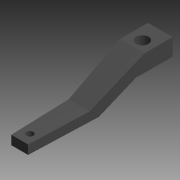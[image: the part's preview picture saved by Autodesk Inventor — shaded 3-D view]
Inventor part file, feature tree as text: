
AUTODESK INVENTOR PART (.ipt)
format: ipt  version: 2015 (Build 190159000, 159)  size: 88,576 bytes
history: native  units: mm (DEFAULTED — no unit token found)
features: chamfer x2, hole x2, extrude x1, sketch x1
ambient origin geometry x8: Origin, YZ Plane, XZ Plane, XY Plane, X Axis, Y Axis, Z Axis, Center Point
bodies: Solid1 (feature_tree)
feature tree (6):
  extrude  "Extrusion1"  Depth=125.0mm
  chamfer  "Chamfer1"  Distance=25.0mm
  chamfer  "Chamfer2"  Distance=30.0mm
  hole  "Hole1"  [1 undecoded]
  hole  "Hole2"  [1 undecoded]
  sketch  "Sketch1"  dims[d0=8.0mm d1=125.0mm d2=25.0mm d3=30.0mm d4=15.0mm d5=27.052603mm d6=22.0mm d7=0.0mm d8=100.0mm d9=3.5mm d10=45.0deg d11=100.0mm d12=3.5mm d13=45.0deg d14=9.0mm d15=11.0mm d16=6.0mm d17=6.0mm d18=4.0mm d19=2.0mm d20=90.0deg d21=8.0mm d22=20.594885mm d23=16.0mm d24=11.0mm d25=11.0mm d26=6.0mm d27=4.0mm d28=2.0mm d29=90.0deg d30=8.0mm d31=20.594885mm]
note: 2 required parameter values undecoded (feature->parameter linkage not recoverable at this tier; creation-order binding heuristic only, values carry confidence <= 0.55)
